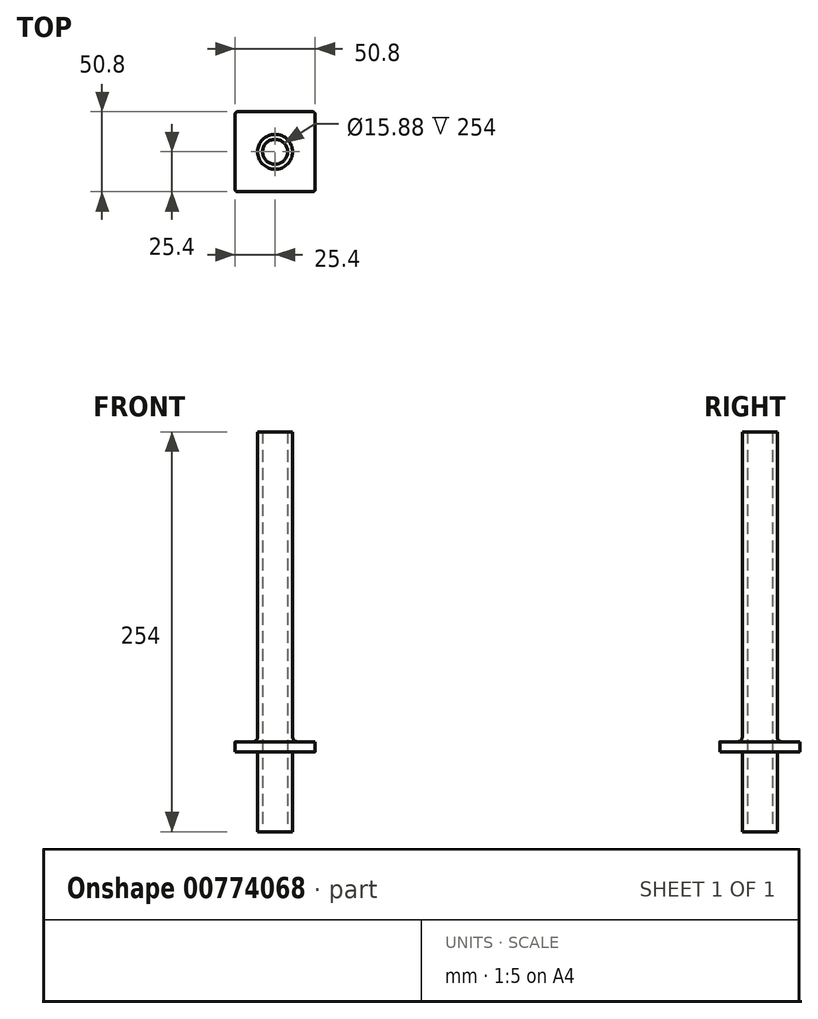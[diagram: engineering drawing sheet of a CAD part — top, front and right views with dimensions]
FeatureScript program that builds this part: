
annotation { "Feature Type Name" : "Feature", "Feature Type Description" : "" }
export const myFeature = defineFeature(function(context is Context, id is Id, definition is map)
    precondition{}
    {
        {
            var Q0;
            Q0=qCreatedBy(makeId("Top.planeOp"),FACE);
            var sketch = newSketch(context, id + "F0", { "sketchPlane" : qUnion([Q0])});
            skCircle(sketch, "E0", {"center": v(0, 0) * mm, "radius": 11.11 * mm});
            skCircle(sketch, "E1", {"center": v(0, 0) * mm, "radius": 7.94 * mm});
            skLineSegment(sketch, "E2", {"start": v(7.94, 0) * mm, "end": v(11.11, 0) * mm});
            skSolve(sketch);
        }
        {
            var Q0;
            Q0=makeQuery(id+"F0.imprint","IMPRINT",FACE,{"disambiguationData":[TD([[makeQuery(id+"F0.imprint","IMPRINT",EDGE,{"derivedFrom":sQuery(id+"F0.wireOp",EDGE,"E0")}),1.0]])]});
            extrude(context, id + "F1", {"entities" : qUnion([Q0]), "depth" : 203.2 * mm, "offsetDistance" : 25.4 * mm, "hasSecondDirection" : true, "secondDirectionOppositeDirection" : true, "secondDirectionDepth" : 50.8 * mm});
        }
        {
            var Q0;
            Q0=qCreatedBy(makeId("Top.planeOp"),FACE);
            var sketch = newSketch(context, id + "F2", { "sketchPlane" : qUnion([Q0])});
            skLineSegment(sketch, "E3.bottom", {"start": v(23.81, 25.4) * mm, "end": v(-23.81, 25.4) * mm});
            skLineSegment(sketch, "E3.top", {"start": v(23.81, -25.4) * mm, "end": v(-23.81, -25.4) * mm});
            skLineSegment(sketch, "E3.left", {"start": v(25.4, 23.81) * mm, "end": v(25.4, -23.81) * mm});
            skLineSegment(sketch, "E3.right", {"start": v(-25.4, 23.81) * mm, "end": v(-25.4, -23.81) * mm});
            skPoint(sketch, "E3.middle", {"position": v(0, 0) * mm});
            skCircle(sketch, "E4.0", {"center": v(0, 0) * mm, "radius": 7.94 * mm});
            skPoint(sketch, "E5.visualSharp", {"position": v(25.4, 25.4) * mm});
            skArc(sketch, "E5.filletArc", {"start": v(25.4, 23.81) * mm, "mid": v(24.94, 24.94) * mm, "end": v(23.81, 25.4) * mm});
            skPoint(sketch, "E6.visualSharp", {"position": v(-25.4, 25.4) * mm});
            skArc(sketch, "E6.filletArc", {"start": v(-23.81, 25.4) * mm, "mid": v(-24.94, 24.94) * mm, "end": v(-25.4, 23.81) * mm});
            skPoint(sketch, "E7.visualSharp", {"position": v(-25.4, -25.4) * mm});
            skArc(sketch, "E7.filletArc", {"start": v(-25.4, -23.81) * mm, "mid": v(-24.94, -24.94) * mm, "end": v(-23.81, -25.4) * mm});
            skPoint(sketch, "E8.visualSharp", {"position": v(25.4, -25.4) * mm});
            skArc(sketch, "E8.filletArc", {"start": v(23.81, -25.4) * mm, "mid": v(24.94, -24.94) * mm, "end": v(25.4, -23.81) * mm});
            skSolve(sketch);
        }
        {
            var Q0;
            Q0=makeQuery(id+"F2.imprint","IMPRINT",FACE,{"disambiguationData":[TD([[makeQuery(id+"F2.imprint","IMPRINT",EDGE,{"derivedFrom":sQuery(id+"F2.wireOp",EDGE,"E3.bottom")}),1.0]])]});
            extrude(context, id + "F3", {"entities" : qUnion([Q0]), "operationType" : NewBodyOperationType.ADD, "depth" : 6.35 * mm, "offsetDistance" : 25.4 * mm});
        }
        {
            var Q0;
            Q0=makeQuery(id+"F3.boolean.opBoolean","INTERSECT",EDGE,{"derivedFrom":[makeQuery(id+"F1.opExtrude","SWEPT_FACE",FACE,{"disambiguationData":[OSD([sQuery(id+"F0.wireOp",EDGE,"E0")])]}),makeQuery(id+"F3.opExtrude","CAP_FACE",FACE,{"disambiguationData":[OSD([sQuery(id+"F2.wireOp",EDGE,"E3.bottom"),sQuery(id+"F2.wireOp",EDGE,"E3.top"),sQuery(id+"F2.wireOp",EDGE,"E3.left"),sQuery(id+"F2.wireOp",EDGE,"E3.right"),sQuery(id+"F2.wireOp",EDGE,"E4.0"),sQuery(id+"F2.wireOp",EDGE,"E5.filletArc"),sQuery(id+"F2.wireOp",EDGE,"E6.filletArc"),sQuery(id+"F2.wireOp",EDGE,"E7.filletArc"),sQuery(id+"F2.wireOp",EDGE,"E8.filletArc")])],"isStart":false})]});
            fillet(context, id + "F4", {"entities" : qUnion([Q0]), "radius" : 3.17 * mm, "tangentPropagation" : true, "allowEdgeOverflow" : false});
        }
    });
